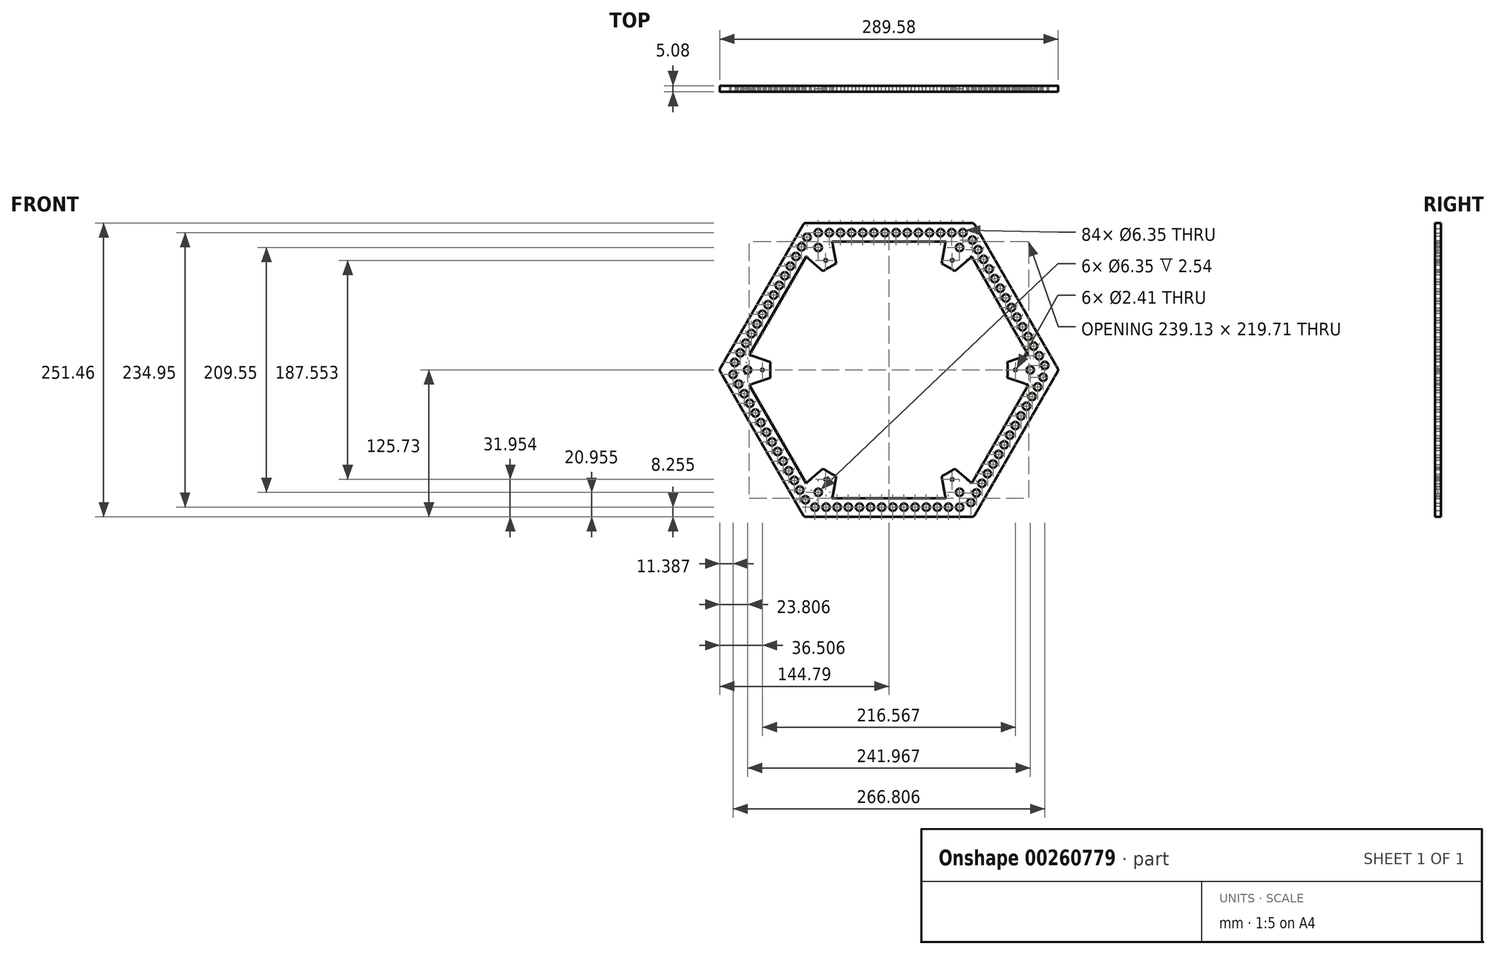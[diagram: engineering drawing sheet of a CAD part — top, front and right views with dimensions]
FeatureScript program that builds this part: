
annotation { "Feature Type Name" : "Feature", "Feature Type Description" : "" }
export const myFeature = defineFeature(function(context is Context, id is Id, definition is map)
    precondition{}
    {
        {
            var Q0;
            Q0=qCreatedBy(makeId("Front.planeOp"),FACE);
            var sketch = newSketch(context, id + "F0", { "sketchPlane" : qUnion([Q0])});
            skCircle(sketch, "E0.cCircle", {"center": v(0, 0) * mm, "radius": 125.73 * mm, "construction": true});
            skLineSegment(sketch, "E0.0", {"start": v(-71.12, 125.73) * mm, "end": v(71.12, 125.73) * mm});
            skLineSegment(sketch, "E0.1", {"start": v(73.32, 124.46) * mm, "end": v(144.45, 1.27) * mm});
            skLineSegment(sketch, "E0.2", {"start": v(144.45, -1.27) * mm, "end": v(73.32, -124.46) * mm});
            skLineSegment(sketch, "E0.3", {"start": v(71.12, -125.73) * mm, "end": v(-71.12, -125.73) * mm});
            skLineSegment(sketch, "E0.4", {"start": v(-73.32, -124.46) * mm, "end": v(-144.45, -1.27) * mm});
            skLineSegment(sketch, "E0.5", {"start": v(-144.45, 1.27) * mm, "end": v(-73.32, 124.46) * mm});
            skPoint(sketch, "E0.0.midPoint", {"position": v(0, 125.73) * mm});
            skCircle(sketch, "E1.cCircle", {"center": v(0, 0) * mm, "radius": 104.78 * mm, "construction": true});
            skLineSegment(sketch, "E1.0", {"start": v(-60.5, 104.78) * mm, "end": v(60.5, 104.78) * mm, "construction": true});
            skLineSegment(sketch, "E1.1", {"start": v(60.5, 104.78) * mm, "end": v(120.98, 0) * mm, "construction": true});
            skLineSegment(sketch, "E1.2", {"start": v(120.98, 0) * mm, "end": v(60.5, -104.78) * mm, "construction": true});
            skLineSegment(sketch, "E1.3", {"start": v(60.5, -104.77) * mm, "end": v(-60.5, -104.78) * mm, "construction": true});
            skLineSegment(sketch, "E1.4", {"start": v(-60.5, -104.78) * mm, "end": v(-120.98, 0) * mm, "construction": true});
            skLineSegment(sketch, "E1.5", {"start": v(-120.98, 0) * mm, "end": v(-60.5, 104.78) * mm, "construction": true});
            skPoint(sketch, "E1.0.midPoint", {"position": v(0, 104.78) * mm});
            skCircle(sketch, "E2.cCircle", {"center": v(0, 0) * mm, "radius": 109.85 * mm, "construction": true});
            skLineSegment(sketch, "E2.0", {"start": v(-63.42, 109.85) * mm, "end": v(63.42, 109.85) * mm});
            skLineSegment(sketch, "E2.1", {"start": v(63.42, 109.85) * mm, "end": v(126.85, 0) * mm});
            skLineSegment(sketch, "E2.2", {"start": v(126.85, 0) * mm, "end": v(63.42, -109.85) * mm});
            skLineSegment(sketch, "E2.3", {"start": v(63.42, -109.85) * mm, "end": v(-63.42, -109.85) * mm});
            skLineSegment(sketch, "E2.4", {"start": v(-63.42, -109.85) * mm, "end": v(-126.85, 0) * mm});
            skLineSegment(sketch, "E2.5", {"start": v(-126.85, 0) * mm, "end": v(-63.42, 109.85) * mm});
            skPoint(sketch, "E2.0.midPoint", {"position": v(0, 109.85) * mm});
            skCircle(sketch, "E3", {"center": v(-60.5, 104.78) * mm, "radius": 3.17 * mm});
            skCircle(sketch, "E4", {"center": v(60.5, 104.78) * mm, "radius": 3.17 * mm});
            skCircle(sketch, "E5", {"center": v(-120.98, 0) * mm, "radius": 3.17 * mm});
            skCircle(sketch, "E6", {"center": v(120.98, 0) * mm, "radius": 3.18 * mm});
            skCircle(sketch, "E7", {"center": v(60.5, -104.78) * mm, "radius": 3.17 * mm});
            skCircle(sketch, "E8", {"center": v(-60.5, -104.78) * mm, "radius": 3.17 * mm});
            skCircle(sketch, "E9", {"center": v(-120.98, 0) * mm, "radius": 12.7 * mm});
            skCircle(sketch, "E10", {"center": v(-60.5, -104.78) * mm, "radius": 12.7 * mm});
            skCircle(sketch, "E11", {"center": v(60.5, -104.77) * mm, "radius": 12.7 * mm});
            skCircle(sketch, "E12", {"center": v(120.98, 0) * mm, "radius": 12.7 * mm});
            skCircle(sketch, "E13", {"center": v(60.5, 104.78) * mm, "radius": 12.7 * mm});
            skCircle(sketch, "E14", {"center": v(-60.5, 104.78) * mm, "radius": 12.7 * mm});
            skLineSegment(sketch, "E15", {"start": v(-66.84, 93.78) * mm, "end": v(-71.24, 96.32) * mm});
            skLineSegment(sketch, "E16", {"start": v(-114.63, 11) * mm, "end": v(-119.03, 13.54) * mm});
            skLineSegment(sketch, "E17", {"start": v(-114.63, -11) * mm, "end": v(-119.03, -13.54) * mm});
            skLineSegment(sketch, "E18", {"start": v(-47.8, -104.78) * mm, "end": v(-47.8, -109.85) * mm});
            skLineSegment(sketch, "E19", {"start": v(47.8, -104.77) * mm, "end": v(47.8, -109.85) * mm});
            skLineSegment(sketch, "E20", {"start": v(66.84, -93.78) * mm, "end": v(71.24, -96.32) * mm});
            skLineSegment(sketch, "E21", {"start": v(114.63, 11) * mm, "end": v(119.03, 13.54) * mm});
            skLineSegment(sketch, "E22", {"start": v(114.63, -11) * mm, "end": v(119.03, -13.54) * mm});
            skLineSegment(sketch, "E23", {"start": v(66.84, 93.78) * mm, "end": v(71.24, 96.32) * mm});
            skLineSegment(sketch, "E24", {"start": v(47.8, 104.78) * mm, "end": v(47.8, 109.85) * mm});
            skLineSegment(sketch, "E25", {"start": v(-47.8, 104.78) * mm, "end": v(-47.8, 109.85) * mm});
            skLineSegment(sketch, "E26", {"start": v(-71.24, -96.32) * mm, "end": v(-66.84, -93.78) * mm});
            skPoint(sketch, "E27.visualSharp", {"position": v(-72.6, 125.73) * mm});
            skArc(sketch, "E27.filletArc", {"start": v(-71.12, 125.73) * mm, "mid": v(-72.4, 125.39) * mm, "end": v(-73.32, 124.46) * mm});
            skPoint(sketch, "E28.visualSharp", {"position": v(72.6, 125.73) * mm});
            skArc(sketch, "E28.filletArc", {"start": v(73.32, 124.46) * mm, "mid": v(72.4, 125.39) * mm, "end": v(71.12, 125.73) * mm});
            skPoint(sketch, "E29.visualSharp", {"position": v(145.18, 0) * mm});
            skArc(sketch, "E29.filletArc", {"start": v(144.45, -1.27) * mm, "mid": v(144.79, 0) * mm, "end": v(144.45, 1.27) * mm});
            skPoint(sketch, "E30.visualSharp", {"position": v(72.6, -125.73) * mm});
            skArc(sketch, "E30.filletArc", {"start": v(71.12, -125.73) * mm, "mid": v(72.4, -125.39) * mm, "end": v(73.32, -124.46) * mm});
            skPoint(sketch, "E31.visualSharp", {"position": v(-72.6, -125.73) * mm});
            skArc(sketch, "E31.filletArc", {"start": v(-73.32, -124.46) * mm, "mid": v(-72.4, -125.39) * mm, "end": v(-71.12, -125.73) * mm});
            skPoint(sketch, "E32.visualSharp", {"position": v(-145.18, 0) * mm});
            skArc(sketch, "E32.filletArc", {"start": v(-144.45, 1.27) * mm, "mid": v(-144.79, 0) * mm, "end": v(-144.45, -1.27) * mm});
            skLineSegment(sketch, "E33", {"start": v(-55.1, 83.45) * mm, "end": v(-68.74, 95.12) * mm});
            skLineSegment(sketch, "E34", {"start": v(48, 107.1) * mm, "end": v(44.72, 89.44) * mm});
            skLineSegment(sketch, "E35", {"start": v(55.1, 83.45) * mm, "end": v(68.74, 95.12) * mm});
            skLineSegment(sketch, "E36", {"start": v(116.75, 11.97) * mm, "end": v(99.82, 5.99) * mm});
            skLineSegment(sketch, "E37", {"start": v(99.82, -5.99) * mm, "end": v(116.75, -11.97) * mm});
            skLineSegment(sketch, "E38", {"start": v(48, -107.1) * mm, "end": v(44.72, -89.44) * mm});
            skLineSegment(sketch, "E39", {"start": v(55.1, -83.45) * mm, "end": v(68.74, -95.12) * mm});
            skLineSegment(sketch, "E40", {"start": v(-48, -107.1) * mm, "end": v(-44.72, -89.44) * mm});
            skLineSegment(sketch, "E41", {"start": v(-55.1, -83.45) * mm, "end": v(-68.74, -95.12) * mm});
            skLineSegment(sketch, "E42", {"start": v(-116.75, 11.97) * mm, "end": v(-99.82, 5.99) * mm});
            skLineSegment(sketch, "E43", {"start": v(-99.82, -5.99) * mm, "end": v(-116.75, -11.97) * mm});
            skLineSegment(sketch, "E44", {"start": v(-41.44, 71.78) * mm, "end": v(-60.5, 104.78) * mm, "construction": true});
            skLineSegment(sketch, "E45", {"start": v(41.44, 71.78) * mm, "end": v(60.5, 104.78) * mm, "construction": true});
            skLineSegment(sketch, "E46", {"start": v(82.88, 0) * mm, "end": v(120.98, 0) * mm, "construction": true});
            skLineSegment(sketch, "E47", {"start": v(60.5, -104.78) * mm, "end": v(41.44, -71.78) * mm, "construction": true});
            skLineSegment(sketch, "E48", {"start": v(-60.5, -104.78) * mm, "end": v(-41.44, -71.78) * mm, "construction": true});
            skLineSegment(sketch, "E49", {"start": v(-120.98, 0) * mm, "end": v(-82.88, 0) * mm, "construction": true});
            skLineSegment(sketch, "E50", {"start": v(-44.72, 89.44) * mm, "end": v(-48, 107.1) * mm});
            skPoint(sketch, "E51.visualSharp", {"position": v(-41.44, 71.78) * mm});
            skArc(sketch, "E51.filletArc", {"start": v(-55.1, 83.45) * mm, "mid": v(-47.8, 82.78) * mm, "end": v(-44.72, 89.44) * mm});
            skPoint(sketch, "E52.visualSharp", {"position": v(41.44, 71.78) * mm});
            skArc(sketch, "E52.filletArc", {"start": v(44.72, 89.44) * mm, "mid": v(47.8, 82.78) * mm, "end": v(55.1, 83.45) * mm});
            skPoint(sketch, "E53.visualSharp", {"position": v(82.88, 0) * mm});
            skArc(sketch, "E53.filletArc", {"start": v(99.82, 5.99) * mm, "mid": v(95.58, 0) * mm, "end": v(99.82, -5.99) * mm});
            skPoint(sketch, "E54.visualSharp", {"position": v(41.44, -71.78) * mm});
            skArc(sketch, "E54.filletArc", {"start": v(55.1, -83.45) * mm, "mid": v(47.8, -82.78) * mm, "end": v(44.72, -89.44) * mm});
            skPoint(sketch, "E55.visualSharp", {"position": v(-41.44, -71.78) * mm});
            skArc(sketch, "E55.filletArc", {"start": v(-44.72, -89.44) * mm, "mid": v(-47.8, -82.78) * mm, "end": v(-55.1, -83.45) * mm});
            skPoint(sketch, "E56.visualSharp", {"position": v(-82.88, 0) * mm});
            skArc(sketch, "E56.filletArc", {"start": v(-99.82, -5.99) * mm, "mid": v(-95.58, 0) * mm, "end": v(-99.82, 5.99) * mm});
            skCircle(sketch, "E57", {"center": v(-108.28, 0) * mm, "radius": 1.2 * mm});
            skCircle(sketch, "E58", {"center": v(-54.14, 93.78) * mm, "radius": 1.2 * mm});
            skCircle(sketch, "E59", {"center": v(54.14, 93.78) * mm, "radius": 1.2 * mm});
            skCircle(sketch, "E60", {"center": v(-54.14, -93.78) * mm, "radius": 1.2 * mm});
            skCircle(sketch, "E61", {"center": v(54.14, -93.78) * mm, "radius": 1.2 * mm});
            skCircle(sketch, "E62", {"center": v(108.28, 0) * mm, "radius": 1.2 * mm});
            skSolve(sketch);
        }
        {
            var Q0;
            Q0=makeQuery(id+"F0.imprint","IMPRINT",FACE,{"disambiguationData":[TD([[makeQuery(id+"F0.imprint","IMPRINT",EDGE,{"derivedFrom":sQuery(id+"F0.wireOp",EDGE,"E3")}),-1.0]])]});
            var Q1;
            {var subQ0=sQuery(id+"F0.wireOp",EDGE,"E2.1");var subQ1=sQuery(id+"F0.wireOp",EDGE,"E2.0");var subQ2=makeQuery(id+"F0.imprint","INTERSECT",VERTEX,{"derivedFrom":[subQ1,subQ0]});Q1=makeQuery(id+"F0.imprint","IMPRINT",FACE,{"disambiguationData":[TD([[makeQuery(id+"F0.imprint","IMPRINT",EDGE,{"disambiguationData":[TD([[subQ2,1.0]])],"derivedFrom":subQ1}),1.0]])]});}
            var Q2;
            Q2=makeQuery(id+"F0.imprint","IMPRINT",FACE,{"disambiguationData":[TD([[makeQuery(id+"F0.imprint","IMPRINT",EDGE,{"derivedFrom":sQuery(id+"F0.wireOp",EDGE,"E4")}),-1.0]])]});
            var Q3;
            {var subQ0=sQuery(id+"F0.wireOp",EDGE,"E2.5");var subQ1=sQuery(id+"F0.wireOp",EDGE,"E2.0");var subQ2=makeQuery(id+"F0.imprint","INTERSECT",VERTEX,{"derivedFrom":[subQ1,subQ0]});Q3=makeQuery(id+"F0.imprint","IMPRINT",FACE,{"disambiguationData":[TD([[makeQuery(id+"F0.imprint","IMPRINT",EDGE,{"disambiguationData":[TD([[subQ2,-1.0]])],"derivedFrom":subQ1}),1.0]])]});}
            var Q4;
            {var subQ0=sQuery(id+"F0.wireOp",EDGE,"E2.5");var subQ1=sQuery(id+"F0.wireOp",EDGE,"E2.4");var subQ2=makeQuery(id+"F0.imprint","INTERSECT",VERTEX,{"derivedFrom":[subQ1,subQ0]});Q4=makeQuery(id+"F0.imprint","IMPRINT",FACE,{"disambiguationData":[TD([[makeQuery(id+"F0.imprint","IMPRINT",EDGE,{"disambiguationData":[TD([[subQ2,1.0]])],"derivedFrom":subQ1}),1.0]])]});}
            var Q5;
            {var subQ0=sQuery(id+"F0.wireOp",EDGE,"E2.4");var subQ1=sQuery(id+"F0.wireOp",EDGE,"E2.3");var subQ2=makeQuery(id+"F0.imprint","INTERSECT",VERTEX,{"derivedFrom":[subQ1,subQ0]});Q5=makeQuery(id+"F0.imprint","IMPRINT",FACE,{"disambiguationData":[TD([[makeQuery(id+"F0.imprint","IMPRINT",EDGE,{"disambiguationData":[TD([[subQ2,1.0]])],"derivedFrom":subQ1}),1.0]])]});}
            var Q6;
            Q6=makeQuery(id+"F0.imprint","IMPRINT",FACE,{"disambiguationData":[TD([[makeQuery(id+"F0.imprint","IMPRINT",EDGE,{"derivedFrom":sQuery(id+"F0.wireOp",EDGE,"E8")}),-1.0]])]});
            var Q7;
            Q7=makeQuery(id+"F0.imprint","IMPRINT",FACE,{"disambiguationData":[TD([[makeQuery(id+"F0.imprint","IMPRINT",EDGE,{"derivedFrom":sQuery(id+"F0.wireOp",EDGE,"E7")}),-1.0]])]});
            var Q8;
            {var subQ0=sQuery(id+"F0.wireOp",EDGE,"E2.3");var subQ1=sQuery(id+"F0.wireOp",EDGE,"E2.2");var subQ2=makeQuery(id+"F0.imprint","INTERSECT",VERTEX,{"derivedFrom":[subQ1,subQ0]});Q8=makeQuery(id+"F0.imprint","IMPRINT",FACE,{"disambiguationData":[TD([[makeQuery(id+"F0.imprint","IMPRINT",EDGE,{"disambiguationData":[TD([[subQ2,1.0]])],"derivedFrom":subQ1}),1.0]])]});}
            var Q9;
            Q9=makeQuery(id+"F0.imprint","IMPRINT",FACE,{"disambiguationData":[TD([[makeQuery(id+"F0.imprint","IMPRINT",EDGE,{"derivedFrom":sQuery(id+"F0.wireOp",EDGE,"E6")}),-1.0]])]});
            var Q10;
            Q10=makeQuery(id+"F0.imprint","IMPRINT",FACE,{"disambiguationData":[TD([[makeQuery(id+"F0.imprint","IMPRINT",EDGE,{"derivedFrom":sQuery(id+"F0.wireOp",EDGE,"E5")}),-1.0]])]});
            var Q11;
            Q11=makeQuery(id+"F0.imprint","IMPRINT",FACE,{"disambiguationData":[TD([[makeQuery(id+"F0.imprint","IMPRINT",EDGE,{"derivedFrom":sQuery(id+"F0.wireOp",EDGE,"E0.0")}),-1.0]])]});
            var Q12;
            {var subQ0=sQuery(id+"F0.wireOp",EDGE,"E2.2");var subQ1=sQuery(id+"F0.wireOp",EDGE,"E2.1");var subQ2=makeQuery(id+"F0.imprint","INTERSECT",VERTEX,{"derivedFrom":[subQ1,subQ0]});Q12=makeQuery(id+"F0.imprint","IMPRINT",FACE,{"disambiguationData":[TD([[makeQuery(id+"F0.imprint","IMPRINT",EDGE,{"disambiguationData":[TD([[subQ2,1.0]])],"derivedFrom":subQ1}),1.0]])]});}
            var Q13;
            {var subQ1=sQuery(id+"F0.wireOp",EDGE,"E36");Q13=makeQuery(id+"F0.imprint","IMPRINT",FACE,{"disambiguationData":[TD([[makeQuery(id+"F0.imprint","IMPRINT",EDGE,{"derivedFrom":subQ1}),1.0]])]});}
            var Q14;
            {var subQ0=sQuery(id+"F0.wireOp",EDGE,"E38");Q14=makeQuery(id+"F0.imprint","IMPRINT",FACE,{"disambiguationData":[TD([[makeQuery(id+"F0.imprint","IMPRINT",EDGE,{"derivedFrom":subQ0}),-1.0]])]});}
            var Q15;
            {var subQ4=sQuery(id+"F0.wireOp",EDGE,"E40");Q15=makeQuery(id+"F0.imprint","IMPRINT",FACE,{"disambiguationData":[TD([[makeQuery(id+"F0.imprint","IMPRINT",EDGE,{"derivedFrom":subQ4}),1.0]])]});}
            var Q16;
            {var subQ0=sQuery(id+"F0.wireOp",EDGE,"E42");Q16=makeQuery(id+"F0.imprint","IMPRINT",FACE,{"disambiguationData":[TD([[makeQuery(id+"F0.imprint","IMPRINT",EDGE,{"derivedFrom":subQ0}),-1.0]])]});}
            var Q17;
            {var subQ0=sQuery(id+"F0.wireOp",EDGE,"E33");Q17=makeQuery(id+"F0.imprint","IMPRINT",FACE,{"disambiguationData":[TD([[makeQuery(id+"F0.imprint","IMPRINT",EDGE,{"derivedFrom":subQ0}),-1.0]])]});}
            var Q18;
            {var subQ4=sQuery(id+"F0.wireOp",EDGE,"E34");Q18=makeQuery(id+"F0.imprint","IMPRINT",FACE,{"disambiguationData":[TD([[makeQuery(id+"F0.imprint","IMPRINT",EDGE,{"derivedFrom":subQ4}),1.0]])]});}
            var Q19;
            {var subQ11=sQuery(id+"F0.wireOp",EDGE,"E51.filletArc");Q19=makeQuery(id+"F0.imprint","IMPRINT",FACE,{"disambiguationData":[TD([[makeQuery(id+"F0.imprint","IMPRINT",EDGE,{"derivedFrom":subQ11}),1.0]])]});}
            var Q20;
            {var subQ12=sQuery(id+"F0.wireOp",EDGE,"E52.filletArc");Q20=makeQuery(id+"F0.imprint","IMPRINT",FACE,{"disambiguationData":[TD([[makeQuery(id+"F0.imprint","IMPRINT",EDGE,{"derivedFrom":subQ12}),1.0]])]});}
            var Q21;
            {var subQ9=sQuery(id+"F0.wireOp",EDGE,"E53.filletArc");Q21=makeQuery(id+"F0.imprint","IMPRINT",FACE,{"disambiguationData":[TD([[makeQuery(id+"F0.imprint","IMPRINT",EDGE,{"derivedFrom":subQ9}),1.0]])]});}
            var Q22;
            {var subQ5=sQuery(id+"F0.wireOp",EDGE,"E55.filletArc");Q22=makeQuery(id+"F0.imprint","IMPRINT",FACE,{"disambiguationData":[TD([[makeQuery(id+"F0.imprint","IMPRINT",EDGE,{"derivedFrom":subQ5}),1.0]])]});}
            var Q23;
            {var subQ5=sQuery(id+"F0.wireOp",EDGE,"E54.filletArc");Q23=makeQuery(id+"F0.imprint","IMPRINT",FACE,{"disambiguationData":[TD([[makeQuery(id+"F0.imprint","IMPRINT",EDGE,{"derivedFrom":subQ5}),1.0]])]});}
            var Q24;
            {var subQ5=sQuery(id+"F0.wireOp",EDGE,"E56.filletArc");Q24=makeQuery(id+"F0.imprint","IMPRINT",FACE,{"disambiguationData":[TD([[makeQuery(id+"F0.imprint","IMPRINT",EDGE,{"derivedFrom":subQ5}),1.0]])]});}
            extrude(context, id + "F1", {"entities" : qUnion([Q0, Q1, Q2, Q3, Q4, Q5, Q6, Q7, Q8, Q9, Q10, Q11, Q12, Q13, Q14, Q15, Q16, Q17, Q18, Q19, Q20, Q21, Q22, Q23, Q24]), "depth" : 5.08 * mm});
        }
        {
            var Q0;
            Q0=makeQuery(id+"F0.imprint","IMPRINT",FACE,{"disambiguationData":[TD([[makeQuery(id+"F0.imprint","IMPRINT",EDGE,{"derivedFrom":sQuery(id+"F0.wireOp",EDGE,"E3")}),1.0]])]});
            var Q1;
            Q1=makeQuery(id+"F0.imprint","IMPRINT",FACE,{"disambiguationData":[TD([[makeQuery(id+"F0.imprint","IMPRINT",EDGE,{"derivedFrom":sQuery(id+"F0.wireOp",EDGE,"E4")}),1.0]])]});
            var Q2;
            Q2=makeQuery(id+"F0.imprint","IMPRINT",FACE,{"disambiguationData":[TD([[makeQuery(id+"F0.imprint","IMPRINT",EDGE,{"derivedFrom":sQuery(id+"F0.wireOp",EDGE,"E5")}),1.0]])]});
            var Q3;
            Q3=makeQuery(id+"F0.imprint","IMPRINT",FACE,{"disambiguationData":[TD([[makeQuery(id+"F0.imprint","IMPRINT",EDGE,{"derivedFrom":sQuery(id+"F0.wireOp",EDGE,"E8")}),1.0]])]});
            var Q4;
            Q4=makeQuery(id+"F0.imprint","IMPRINT",FACE,{"disambiguationData":[TD([[makeQuery(id+"F0.imprint","IMPRINT",EDGE,{"derivedFrom":sQuery(id+"F0.wireOp",EDGE,"E7")}),1.0]])]});
            var Q5;
            Q5=makeQuery(id+"F0.imprint","IMPRINT",FACE,{"disambiguationData":[TD([[makeQuery(id+"F0.imprint","IMPRINT",EDGE,{"derivedFrom":sQuery(id+"F0.wireOp",EDGE,"E6")}),1.0]])]});
            extrude(context, id + "F2", {"entities" : qUnion([Q0, Q1, Q2, Q3, Q4, Q5]), "operationType" : NewBodyOperationType.ADD, "depth" : 2.54 * mm});
        }
        {
            var Q0;
            Q0=makeQuery(id+"F1.opExtrude","CAP_FACE",FACE,{"disambiguationData":[OSD([sQuery(id+"F0.wireOp",EDGE,"E0.0"),sQuery(id+"F0.wireOp",EDGE,"E0.1"),sQuery(id+"F0.wireOp",EDGE,"E0.2"),sQuery(id+"F0.wireOp",EDGE,"E0.3"),sQuery(id+"F0.wireOp",EDGE,"E0.4"),sQuery(id+"F0.wireOp",EDGE,"E0.5"),sQuery(id+"F0.wireOp",EDGE,"E2.0"),sQuery(id+"F0.wireOp",EDGE,"E2.1"),sQuery(id+"F0.wireOp",EDGE,"E2.2"),sQuery(id+"F0.wireOp",EDGE,"E2.3"),sQuery(id+"F0.wireOp",EDGE,"E2.4"),sQuery(id+"F0.wireOp",EDGE,"E2.5"),sQuery(id+"F0.wireOp",EDGE,"E3"),sQuery(id+"F0.wireOp",EDGE,"E4"),sQuery(id+"F0.wireOp",EDGE,"E5"),sQuery(id+"F0.wireOp",EDGE,"E6"),sQuery(id+"F0.wireOp",EDGE,"E7"),sQuery(id+"F0.wireOp",EDGE,"E8"),sQuery(id+"F0.wireOp",EDGE,"E9"),sQuery(id+"F0.wireOp",EDGE,"E10"),sQuery(id+"F0.wireOp",EDGE,"E11"),sQuery(id+"F0.wireOp",EDGE,"E12"),sQuery(id+"F0.wireOp",EDGE,"E13"),sQuery(id+"F0.wireOp",EDGE,"E14"),sQuery(id+"F0.wireOp",EDGE,"E17"),sQuery(id+"F0.wireOp",EDGE,"E20"),sQuery(id+"F0.wireOp",EDGE,"E22"),sQuery(id+"F0.wireOp",EDGE,"E23"),sQuery(id+"F0.wireOp",EDGE,"E25"),sQuery(id+"F0.wireOp",EDGE,"E26"),sQuery(id+"F0.wireOp",EDGE,"E27.filletArc"),sQuery(id+"F0.wireOp",EDGE,"E28.filletArc"),sQuery(id+"F0.wireOp",EDGE,"E29.filletArc"),sQuery(id+"F0.wireOp",EDGE,"E30.filletArc"),sQuery(id+"F0.wireOp",EDGE,"E31.filletArc"),sQuery(id+"F0.wireOp",EDGE,"E32.filletArc"),sQuery(id+"F0.wireOp",EDGE,"E33"),sQuery(id+"F0.wireOp",EDGE,"E34"),sQuery(id+"F0.wireOp",EDGE,"E35"),sQuery(id+"F0.wireOp",EDGE,"E36"),sQuery(id+"F0.wireOp",EDGE,"E37"),sQuery(id+"F0.wireOp",EDGE,"E38"),sQuery(id+"F0.wireOp",EDGE,"E39"),sQuery(id+"F0.wireOp",EDGE,"E40"),sQuery(id+"F0.wireOp",EDGE,"E41"),sQuery(id+"F0.wireOp",EDGE,"E42"),sQuery(id+"F0.wireOp",EDGE,"E43"),sQuery(id+"F0.wireOp",EDGE,"E50"),sQuery(id+"F0.wireOp",EDGE,"E51.filletArc"),sQuery(id+"F0.wireOp",EDGE,"E52.filletArc"),sQuery(id+"F0.wireOp",EDGE,"E53.filletArc"),sQuery(id+"F0.wireOp",EDGE,"E54.filletArc"),sQuery(id+"F0.wireOp",EDGE,"E55.filletArc"),sQuery(id+"F0.wireOp",EDGE,"E56.filletArc"),sQuery(id+"F0.wireOp",EDGE,"E57"),sQuery(id+"F0.wireOp",EDGE,"E58"),sQuery(id+"F0.wireOp",EDGE,"E59"),sQuery(id+"F0.wireOp",EDGE,"E60"),sQuery(id+"F0.wireOp",EDGE,"E61"),sQuery(id+"F0.wireOp",EDGE,"E62")])],"isStart":false});
            var sketch = newSketch(context, id + "F3", { "sketchPlane" : qUnion([Q0])});
            skCircle(sketch, "E63.cCircle", {"center": v(0, 0) * mm, "radius": 117.48 * mm, "construction": true});
            skLineSegment(sketch, "E63.0", {"start": v(-67.82, 117.47) * mm, "end": v(67.82, 117.48) * mm, "construction": true});
            skLineSegment(sketch, "E63.1", {"start": v(67.82, 117.47) * mm, "end": v(135.65, 0) * mm, "construction": true});
            skLineSegment(sketch, "E63.2", {"start": v(135.65, 0) * mm, "end": v(67.82, -117.47) * mm, "construction": true});
            skLineSegment(sketch, "E63.3", {"start": v(67.82, -117.47) * mm, "end": v(-67.82, -117.48) * mm, "construction": true});
            skLineSegment(sketch, "E63.4", {"start": v(-67.82, -117.48) * mm, "end": v(-135.65, 0) * mm, "construction": true});
            skLineSegment(sketch, "E63.5", {"start": v(-135.65, 0) * mm, "end": v(-67.82, 117.47) * mm, "construction": true});
            skPoint(sketch, "E63.0.midPoint", {"position": v(0, 117.48) * mm});
            skCircle(sketch, "E64", {"center": v(-60.5, 117.48) * mm, "radius": 3.18 * mm});
            skPoint(sketch, "E65", {"position": v(-60.5, 104.78) * mm});
            skCircle(sketch, "E66.1.0.0", {"center": v(-50.97, 117.47) * mm, "radius": 3.18 * mm});
            skCircle(sketch, "E66.2.0.0", {"center": v(-41.44, 117.48) * mm, "radius": 3.18 * mm});
            skCircle(sketch, "E66.3.0.0", {"center": v(-31.92, 117.48) * mm, "radius": 3.18 * mm});
            skCircle(sketch, "E66.4.0.0", {"center": v(-22.4, 117.48) * mm, "radius": 3.18 * mm});
            skCircle(sketch, "E66.5.0.0", {"center": v(-12.87, 117.48) * mm, "radius": 3.18 * mm});
            skCircle(sketch, "E66.6.0.0", {"center": v(-3.34, 117.48) * mm, "radius": 3.18 * mm});
            skCircle(sketch, "E66.7.0.0", {"center": v(6.18, 117.48) * mm, "radius": 3.18 * mm});
            skCircle(sketch, "E66.8.0.0", {"center": v(15.7, 117.48) * mm, "radius": 3.18 * mm});
            skCircle(sketch, "E66.9.0.0", {"center": v(25.23, 117.48) * mm, "radius": 3.18 * mm});
            skCircle(sketch, "E66.10.0.0", {"center": v(34.76, 117.48) * mm, "radius": 3.18 * mm});
            skCircle(sketch, "E66.11.0.0", {"center": v(44.28, 117.48) * mm, "radius": 3.18 * mm});
            skCircle(sketch, "E66.12.0.0", {"center": v(53.8, 117.48) * mm, "radius": 3.18 * mm});
            skCircle(sketch, "E66.13.0.0", {"center": v(63.33, 117.48) * mm, "radius": 3.18 * mm});
            skLineSegment(sketch, "E66.direction1", {"start": v(-60.5, 117.48) * mm, "end": v(-50.97, 117.48) * mm, "construction": true});
            skCircle(sketch, "E67.1.0", {"center": v(-131.98, 6.35) * mm, "radius": 3.18 * mm});
            skCircle(sketch, "E67.1.1", {"center": v(-127.22, 14.6) * mm, "radius": 3.18 * mm});
            skCircle(sketch, "E67.1.2", {"center": v(-122.46, 22.85) * mm, "radius": 3.18 * mm});
            skCircle(sketch, "E67.1.3", {"center": v(-117.7, 31.1) * mm, "radius": 3.18 * mm});
            skCircle(sketch, "E67.1.4", {"center": v(-112.93, 39.35) * mm, "radius": 3.18 * mm});
            skCircle(sketch, "E67.1.5", {"center": v(-108.17, 47.6) * mm, "radius": 3.18 * mm});
            skCircle(sketch, "E67.1.6", {"center": v(-103.4, 55.84) * mm, "radius": 3.18 * mm});
            skCircle(sketch, "E67.1.7", {"center": v(-98.64, 64.1) * mm, "radius": 3.18 * mm});
            skCircle(sketch, "E67.1.8", {"center": v(-93.88, 72.34) * mm, "radius": 3.18 * mm});
            skCircle(sketch, "E67.1.9", {"center": v(-89.12, 80.6) * mm, "radius": 3.18 * mm});
            skCircle(sketch, "E67.1.10", {"center": v(-84.36, 88.84) * mm, "radius": 3.18 * mm});
            skCircle(sketch, "E67.1.11", {"center": v(-79.6, 97.09) * mm, "radius": 3.18 * mm});
            skCircle(sketch, "E67.1.12", {"center": v(-74.83, 105.34) * mm, "radius": 3.18 * mm});
            skCircle(sketch, "E67.1.13", {"center": v(-70.07, 113.59) * mm, "radius": 3.18 * mm});
            skCircle(sketch, "E67.2.0", {"center": v(-71.5, -111.12) * mm, "radius": 3.18 * mm});
            skCircle(sketch, "E67.2.1", {"center": v(-76.25, -102.88) * mm, "radius": 3.18 * mm});
            skCircle(sketch, "E67.2.2", {"center": v(-81.02, -94.63) * mm, "radius": 3.18 * mm});
            skCircle(sketch, "E67.2.3", {"center": v(-85.78, -86.38) * mm, "radius": 3.18 * mm});
            skCircle(sketch, "E67.2.4", {"center": v(-90.54, -78.13) * mm, "radius": 3.18 * mm});
            skCircle(sketch, "E67.2.5", {"center": v(-95.3, -69.88) * mm, "radius": 3.18 * mm});
            skCircle(sketch, "E67.2.6", {"center": v(-100.07, -61.63) * mm, "radius": 3.18 * mm});
            skCircle(sketch, "E67.2.7", {"center": v(-104.83, -53.38) * mm, "radius": 3.18 * mm});
            skCircle(sketch, "E67.2.8", {"center": v(-109.6, -45.13) * mm, "radius": 3.18 * mm});
            skCircle(sketch, "E67.2.9", {"center": v(-114.35, -36.88) * mm, "radius": 3.18 * mm});
            skCircle(sketch, "E67.2.10", {"center": v(-119.12, -28.64) * mm, "radius": 3.18 * mm});
            skCircle(sketch, "E67.2.11", {"center": v(-123.88, -20.39) * mm, "radius": 3.18 * mm});
            skCircle(sketch, "E67.2.12", {"center": v(-128.64, -12.14) * mm, "radius": 3.18 * mm});
            skCircle(sketch, "E67.2.13", {"center": v(-133.4, -3.89) * mm, "radius": 3.18 * mm});
            skCircle(sketch, "E67.3.0", {"center": v(60.5, -117.48) * mm, "radius": 3.18 * mm});
            skCircle(sketch, "E67.3.1", {"center": v(50.97, -117.48) * mm, "radius": 3.18 * mm});
            skCircle(sketch, "E67.3.2", {"center": v(41.44, -117.48) * mm, "radius": 3.18 * mm});
            skCircle(sketch, "E67.3.3", {"center": v(31.92, -117.48) * mm, "radius": 3.18 * mm});
            skCircle(sketch, "E67.3.4", {"center": v(22.4, -117.48) * mm, "radius": 3.18 * mm});
            skCircle(sketch, "E67.3.5", {"center": v(12.87, -117.48) * mm, "radius": 3.18 * mm});
            skCircle(sketch, "E67.3.6", {"center": v(3.34, -117.48) * mm, "radius": 3.18 * mm});
            skCircle(sketch, "E67.3.7", {"center": v(-6.18, -117.48) * mm, "radius": 3.18 * mm});
            skCircle(sketch, "E67.3.8", {"center": v(-15.7, -117.48) * mm, "radius": 3.18 * mm});
            skCircle(sketch, "E67.3.9", {"center": v(-25.23, -117.48) * mm, "radius": 3.18 * mm});
            skCircle(sketch, "E67.3.10", {"center": v(-34.76, -117.48) * mm, "radius": 3.18 * mm});
            skCircle(sketch, "E67.3.11", {"center": v(-44.28, -117.48) * mm, "radius": 3.18 * mm});
            skCircle(sketch, "E67.3.12", {"center": v(-53.8, -117.48) * mm, "radius": 3.18 * mm});
            skCircle(sketch, "E67.3.13", {"center": v(-63.33, -117.48) * mm, "radius": 3.18 * mm});
            skCircle(sketch, "E67.4.0", {"center": v(131.98, -6.35) * mm, "radius": 3.18 * mm});
            skCircle(sketch, "E67.4.1", {"center": v(127.22, -14.6) * mm, "radius": 3.18 * mm});
            skCircle(sketch, "E67.4.2", {"center": v(122.46, -22.85) * mm, "radius": 3.18 * mm});
            skCircle(sketch, "E67.4.3", {"center": v(117.7, -31.1) * mm, "radius": 3.18 * mm});
            skCircle(sketch, "E67.4.4", {"center": v(112.93, -39.35) * mm, "radius": 3.18 * mm});
            skCircle(sketch, "E67.4.5", {"center": v(108.17, -47.6) * mm, "radius": 3.18 * mm});
            skCircle(sketch, "E67.4.6", {"center": v(103.4, -55.84) * mm, "radius": 3.18 * mm});
            skCircle(sketch, "E67.4.7", {"center": v(98.64, -64.1) * mm, "radius": 3.18 * mm});
            skCircle(sketch, "E67.4.8", {"center": v(93.88, -72.34) * mm, "radius": 3.18 * mm});
            skCircle(sketch, "E67.4.9", {"center": v(89.12, -80.6) * mm, "radius": 3.18 * mm});
            skCircle(sketch, "E67.4.10", {"center": v(84.36, -88.84) * mm, "radius": 3.18 * mm});
            skCircle(sketch, "E67.4.11", {"center": v(79.6, -97.09) * mm, "radius": 3.18 * mm});
            skCircle(sketch, "E67.4.12", {"center": v(74.83, -105.34) * mm, "radius": 3.18 * mm});
            skCircle(sketch, "E67.4.13", {"center": v(70.07, -113.59) * mm, "radius": 3.18 * mm});
            skCircle(sketch, "E67.5.0", {"center": v(71.5, 111.13) * mm, "radius": 3.18 * mm});
            skCircle(sketch, "E67.5.1", {"center": v(76.25, 102.88) * mm, "radius": 3.18 * mm});
            skCircle(sketch, "E67.5.2", {"center": v(81.02, 94.63) * mm, "radius": 3.18 * mm});
            skCircle(sketch, "E67.5.3", {"center": v(85.78, 86.38) * mm, "radius": 3.18 * mm});
            skCircle(sketch, "E67.5.4", {"center": v(90.54, 78.13) * mm, "radius": 3.18 * mm});
            skCircle(sketch, "E67.5.5", {"center": v(95.3, 69.88) * mm, "radius": 3.18 * mm});
            skCircle(sketch, "E67.5.6", {"center": v(100.07, 61.63) * mm, "radius": 3.18 * mm});
            skCircle(sketch, "E67.5.7", {"center": v(104.83, 53.38) * mm, "radius": 3.18 * mm});
            skCircle(sketch, "E67.5.8", {"center": v(109.6, 45.13) * mm, "radius": 3.18 * mm});
            skCircle(sketch, "E67.5.9", {"center": v(114.35, 36.88) * mm, "radius": 3.18 * mm});
            skCircle(sketch, "E67.5.10", {"center": v(119.12, 28.64) * mm, "radius": 3.18 * mm});
            skCircle(sketch, "E67.5.11", {"center": v(123.88, 20.39) * mm, "radius": 3.18 * mm});
            skCircle(sketch, "E67.5.12", {"center": v(128.64, 12.14) * mm, "radius": 3.18 * mm});
            skCircle(sketch, "E67.5.13", {"center": v(133.4, 3.89) * mm, "radius": 3.18 * mm});
            skSolve(sketch);
        }
        {
            var Q0;
            Q0 = qSketchRegion(id + "F3", true);
            var Q1;
            {var subQ0=sQuery(id+"F0.wireOp",EDGE,"E8");var subQ1=sQuery(id+"F0.wireOp",EDGE,"E7");var subQ2=sQuery(id+"F0.wireOp",EDGE,"E6");var subQ3=sQuery(id+"F0.wireOp",EDGE,"E5");var subQ4=sQuery(id+"F0.wireOp",EDGE,"E4");var subQ5=sQuery(id+"F0.wireOp",EDGE,"E3");Q1=makeQuery(id+"F2.boolean.opBoolean","MERGE",FACE,{"derivedFrom":[makeQuery(id+"F1.opExtrude","CAP_FACE",FACE,{"disambiguationData":[OSD([sQuery(id+"F0.wireOp",EDGE,"E0.0"),sQuery(id+"F0.wireOp",EDGE,"E0.1"),sQuery(id+"F0.wireOp",EDGE,"E0.2"),sQuery(id+"F0.wireOp",EDGE,"E0.3"),sQuery(id+"F0.wireOp",EDGE,"E0.4"),sQuery(id+"F0.wireOp",EDGE,"E0.5"),sQuery(id+"F0.wireOp",EDGE,"E2.0"),sQuery(id+"F0.wireOp",EDGE,"E2.1"),sQuery(id+"F0.wireOp",EDGE,"E2.2"),sQuery(id+"F0.wireOp",EDGE,"E2.3"),sQuery(id+"F0.wireOp",EDGE,"E2.4"),sQuery(id+"F0.wireOp",EDGE,"E2.5"),subQ5,subQ4,subQ3,subQ2,subQ1,subQ0,sQuery(id+"F0.wireOp",EDGE,"E9"),sQuery(id+"F0.wireOp",EDGE,"E10"),sQuery(id+"F0.wireOp",EDGE,"E11"),sQuery(id+"F0.wireOp",EDGE,"E12"),sQuery(id+"F0.wireOp",EDGE,"E13"),sQuery(id+"F0.wireOp",EDGE,"E14"),sQuery(id+"F0.wireOp",EDGE,"E17"),sQuery(id+"F0.wireOp",EDGE,"E20"),sQuery(id+"F0.wireOp",EDGE,"E22"),sQuery(id+"F0.wireOp",EDGE,"E23"),sQuery(id+"F0.wireOp",EDGE,"E25"),sQuery(id+"F0.wireOp",EDGE,"E26"),sQuery(id+"F0.wireOp",EDGE,"E27.filletArc"),sQuery(id+"F0.wireOp",EDGE,"E28.filletArc"),sQuery(id+"F0.wireOp",EDGE,"E29.filletArc"),sQuery(id+"F0.wireOp",EDGE,"E30.filletArc"),sQuery(id+"F0.wireOp",EDGE,"E31.filletArc"),sQuery(id+"F0.wireOp",EDGE,"E32.filletArc"),sQuery(id+"F0.wireOp",EDGE,"E33"),sQuery(id+"F0.wireOp",EDGE,"E34"),sQuery(id+"F0.wireOp",EDGE,"E35"),sQuery(id+"F0.wireOp",EDGE,"E36"),sQuery(id+"F0.wireOp",EDGE,"E37"),sQuery(id+"F0.wireOp",EDGE,"E38"),sQuery(id+"F0.wireOp",EDGE,"E39"),sQuery(id+"F0.wireOp",EDGE,"E40"),sQuery(id+"F0.wireOp",EDGE,"E41"),sQuery(id+"F0.wireOp",EDGE,"E42"),sQuery(id+"F0.wireOp",EDGE,"E43"),sQuery(id+"F0.wireOp",EDGE,"E50"),sQuery(id+"F0.wireOp",EDGE,"E51.filletArc"),sQuery(id+"F0.wireOp",EDGE,"E52.filletArc"),sQuery(id+"F0.wireOp",EDGE,"E53.filletArc"),sQuery(id+"F0.wireOp",EDGE,"E54.filletArc"),sQuery(id+"F0.wireOp",EDGE,"E55.filletArc"),sQuery(id+"F0.wireOp",EDGE,"E56.filletArc"),sQuery(id+"F0.wireOp",EDGE,"E57"),sQuery(id+"F0.wireOp",EDGE,"E58"),sQuery(id+"F0.wireOp",EDGE,"E59"),sQuery(id+"F0.wireOp",EDGE,"E60"),sQuery(id+"F0.wireOp",EDGE,"E61"),sQuery(id+"F0.wireOp",EDGE,"E62")])],"isStart":true}),makeQuery(id+"F2.opExtrude","CAP_FACE",FACE,{"disambiguationData":[OSD([subQ5])],"isStart":true}),makeQuery(id+"F2.opExtrude","CAP_FACE",FACE,{"disambiguationData":[OSD([subQ4])],"isStart":true}),makeQuery(id+"F2.opExtrude","CAP_FACE",FACE,{"disambiguationData":[OSD([subQ3])],"isStart":true}),makeQuery(id+"F2.opExtrude","CAP_FACE",FACE,{"disambiguationData":[OSD([subQ2])],"isStart":true}),makeQuery(id+"F2.opExtrude","CAP_FACE",FACE,{"disambiguationData":[OSD([subQ1])],"isStart":true}),makeQuery(id+"F2.opExtrude","CAP_FACE",FACE,{"disambiguationData":[OSD([subQ0])],"isStart":true})]});}
            extrude(context, id + "F4", {"entities" : qUnion([Q0]), "operationType" : NewBodyOperationType.REMOVE, "endBound" : BoundingType.UP_TO_SURFACE, "oppositeDirection" : true, "endBoundEntityFace" : qUnion([Q1]), "depth" : 25.4 * mm});
        }
        {
            var Q0;
            Q0=makeQuery(id+"F1.opExtrude","CAP_FACE",FACE,{"disambiguationData":[OSD([sQuery(id+"F0.wireOp",EDGE,"E0.0"),sQuery(id+"F0.wireOp",EDGE,"E0.1"),sQuery(id+"F0.wireOp",EDGE,"E0.2"),sQuery(id+"F0.wireOp",EDGE,"E0.3"),sQuery(id+"F0.wireOp",EDGE,"E0.4"),sQuery(id+"F0.wireOp",EDGE,"E0.5"),sQuery(id+"F0.wireOp",EDGE,"E2.0"),sQuery(id+"F0.wireOp",EDGE,"E2.1"),sQuery(id+"F0.wireOp",EDGE,"E2.2"),sQuery(id+"F0.wireOp",EDGE,"E2.3"),sQuery(id+"F0.wireOp",EDGE,"E2.4"),sQuery(id+"F0.wireOp",EDGE,"E2.5"),sQuery(id+"F0.wireOp",EDGE,"E3"),sQuery(id+"F0.wireOp",EDGE,"E4"),sQuery(id+"F0.wireOp",EDGE,"E5"),sQuery(id+"F0.wireOp",EDGE,"E6"),sQuery(id+"F0.wireOp",EDGE,"E7"),sQuery(id+"F0.wireOp",EDGE,"E8"),sQuery(id+"F0.wireOp",EDGE,"E9"),sQuery(id+"F0.wireOp",EDGE,"E10"),sQuery(id+"F0.wireOp",EDGE,"E11"),sQuery(id+"F0.wireOp",EDGE,"E12"),sQuery(id+"F0.wireOp",EDGE,"E13"),sQuery(id+"F0.wireOp",EDGE,"E14"),sQuery(id+"F0.wireOp",EDGE,"E17"),sQuery(id+"F0.wireOp",EDGE,"E20"),sQuery(id+"F0.wireOp",EDGE,"E22"),sQuery(id+"F0.wireOp",EDGE,"E23"),sQuery(id+"F0.wireOp",EDGE,"E25"),sQuery(id+"F0.wireOp",EDGE,"E26"),sQuery(id+"F0.wireOp",EDGE,"E27.filletArc"),sQuery(id+"F0.wireOp",EDGE,"E28.filletArc"),sQuery(id+"F0.wireOp",EDGE,"E29.filletArc"),sQuery(id+"F0.wireOp",EDGE,"E30.filletArc"),sQuery(id+"F0.wireOp",EDGE,"E31.filletArc"),sQuery(id+"F0.wireOp",EDGE,"E32.filletArc"),sQuery(id+"F0.wireOp",EDGE,"E33"),sQuery(id+"F0.wireOp",EDGE,"E34"),sQuery(id+"F0.wireOp",EDGE,"E35"),sQuery(id+"F0.wireOp",EDGE,"E36"),sQuery(id+"F0.wireOp",EDGE,"E37"),sQuery(id+"F0.wireOp",EDGE,"E38"),sQuery(id+"F0.wireOp",EDGE,"E39"),sQuery(id+"F0.wireOp",EDGE,"E40"),sQuery(id+"F0.wireOp",EDGE,"E41"),sQuery(id+"F0.wireOp",EDGE,"E42"),sQuery(id+"F0.wireOp",EDGE,"E43"),sQuery(id+"F0.wireOp",EDGE,"E50"),sQuery(id+"F0.wireOp",EDGE,"E51.filletArc"),sQuery(id+"F0.wireOp",EDGE,"E52.filletArc"),sQuery(id+"F0.wireOp",EDGE,"E53.filletArc"),sQuery(id+"F0.wireOp",EDGE,"E54.filletArc"),sQuery(id+"F0.wireOp",EDGE,"E55.filletArc"),sQuery(id+"F0.wireOp",EDGE,"E56.filletArc"),sQuery(id+"F0.wireOp",EDGE,"E57"),sQuery(id+"F0.wireOp",EDGE,"E58"),sQuery(id+"F0.wireOp",EDGE,"E59"),sQuery(id+"F0.wireOp",EDGE,"E60"),sQuery(id+"F0.wireOp",EDGE,"E61"),sQuery(id+"F0.wireOp",EDGE,"E62")])],"isStart":false});
            var sketch = newSketch(context, id + "F5", { "sketchPlane" : qUnion([Q0])});
            skCircle(sketch, "E68", {"center": v(0, 0) * mm, "radius": 101.6 * mm});
            skSolve(sketch);
        }
        {
            var Q0;
            Q0 = qSketchRegion(id + "F5", true);
            var Q1;
            {var subQ0=sQuery(id+"F0.wireOp",EDGE,"E8");var subQ1=sQuery(id+"F0.wireOp",EDGE,"E7");var subQ2=sQuery(id+"F0.wireOp",EDGE,"E6");var subQ3=sQuery(id+"F0.wireOp",EDGE,"E5");var subQ4=sQuery(id+"F0.wireOp",EDGE,"E4");var subQ5=sQuery(id+"F0.wireOp",EDGE,"E3");Q1=makeQuery(id+"F2.boolean.opBoolean","MERGE",FACE,{"derivedFrom":[makeQuery(id+"F1.opExtrude","CAP_FACE",FACE,{"disambiguationData":[OSD([sQuery(id+"F0.wireOp",EDGE,"E0.0"),sQuery(id+"F0.wireOp",EDGE,"E0.1"),sQuery(id+"F0.wireOp",EDGE,"E0.2"),sQuery(id+"F0.wireOp",EDGE,"E0.3"),sQuery(id+"F0.wireOp",EDGE,"E0.4"),sQuery(id+"F0.wireOp",EDGE,"E0.5"),sQuery(id+"F0.wireOp",EDGE,"E2.0"),sQuery(id+"F0.wireOp",EDGE,"E2.1"),sQuery(id+"F0.wireOp",EDGE,"E2.2"),sQuery(id+"F0.wireOp",EDGE,"E2.3"),sQuery(id+"F0.wireOp",EDGE,"E2.4"),sQuery(id+"F0.wireOp",EDGE,"E2.5"),subQ5,subQ4,subQ3,subQ2,subQ1,subQ0,sQuery(id+"F0.wireOp",EDGE,"E9"),sQuery(id+"F0.wireOp",EDGE,"E10"),sQuery(id+"F0.wireOp",EDGE,"E11"),sQuery(id+"F0.wireOp",EDGE,"E12"),sQuery(id+"F0.wireOp",EDGE,"E13"),sQuery(id+"F0.wireOp",EDGE,"E14"),sQuery(id+"F0.wireOp",EDGE,"E17"),sQuery(id+"F0.wireOp",EDGE,"E20"),sQuery(id+"F0.wireOp",EDGE,"E22"),sQuery(id+"F0.wireOp",EDGE,"E23"),sQuery(id+"F0.wireOp",EDGE,"E25"),sQuery(id+"F0.wireOp",EDGE,"E26"),sQuery(id+"F0.wireOp",EDGE,"E27.filletArc"),sQuery(id+"F0.wireOp",EDGE,"E28.filletArc"),sQuery(id+"F0.wireOp",EDGE,"E29.filletArc"),sQuery(id+"F0.wireOp",EDGE,"E30.filletArc"),sQuery(id+"F0.wireOp",EDGE,"E31.filletArc"),sQuery(id+"F0.wireOp",EDGE,"E32.filletArc"),sQuery(id+"F0.wireOp",EDGE,"E33"),sQuery(id+"F0.wireOp",EDGE,"E34"),sQuery(id+"F0.wireOp",EDGE,"E35"),sQuery(id+"F0.wireOp",EDGE,"E36"),sQuery(id+"F0.wireOp",EDGE,"E37"),sQuery(id+"F0.wireOp",EDGE,"E38"),sQuery(id+"F0.wireOp",EDGE,"E39"),sQuery(id+"F0.wireOp",EDGE,"E40"),sQuery(id+"F0.wireOp",EDGE,"E41"),sQuery(id+"F0.wireOp",EDGE,"E42"),sQuery(id+"F0.wireOp",EDGE,"E43"),sQuery(id+"F0.wireOp",EDGE,"E50"),sQuery(id+"F0.wireOp",EDGE,"E51.filletArc"),sQuery(id+"F0.wireOp",EDGE,"E52.filletArc"),sQuery(id+"F0.wireOp",EDGE,"E53.filletArc"),sQuery(id+"F0.wireOp",EDGE,"E54.filletArc"),sQuery(id+"F0.wireOp",EDGE,"E55.filletArc"),sQuery(id+"F0.wireOp",EDGE,"E56.filletArc"),sQuery(id+"F0.wireOp",EDGE,"E57"),sQuery(id+"F0.wireOp",EDGE,"E58"),sQuery(id+"F0.wireOp",EDGE,"E59"),sQuery(id+"F0.wireOp",EDGE,"E60"),sQuery(id+"F0.wireOp",EDGE,"E61"),sQuery(id+"F0.wireOp",EDGE,"E62")])],"isStart":true}),makeQuery(id+"F2.opExtrude","CAP_FACE",FACE,{"disambiguationData":[OSD([subQ5])],"isStart":true}),makeQuery(id+"F2.opExtrude","CAP_FACE",FACE,{"disambiguationData":[OSD([subQ4])],"isStart":true}),makeQuery(id+"F2.opExtrude","CAP_FACE",FACE,{"disambiguationData":[OSD([subQ3])],"isStart":true}),makeQuery(id+"F2.opExtrude","CAP_FACE",FACE,{"disambiguationData":[OSD([subQ2])],"isStart":true}),makeQuery(id+"F2.opExtrude","CAP_FACE",FACE,{"disambiguationData":[OSD([subQ1])],"isStart":true}),makeQuery(id+"F2.opExtrude","CAP_FACE",FACE,{"disambiguationData":[OSD([subQ0])],"isStart":true})]});}
            extrude(context, id + "F6", {"entities" : qUnion([Q0]), "operationType" : NewBodyOperationType.REMOVE, "endBound" : BoundingType.UP_TO_SURFACE, "oppositeDirection" : true, "endBoundEntityFace" : qUnion([Q1]), "depth" : 25.4 * mm});
        }
    });
